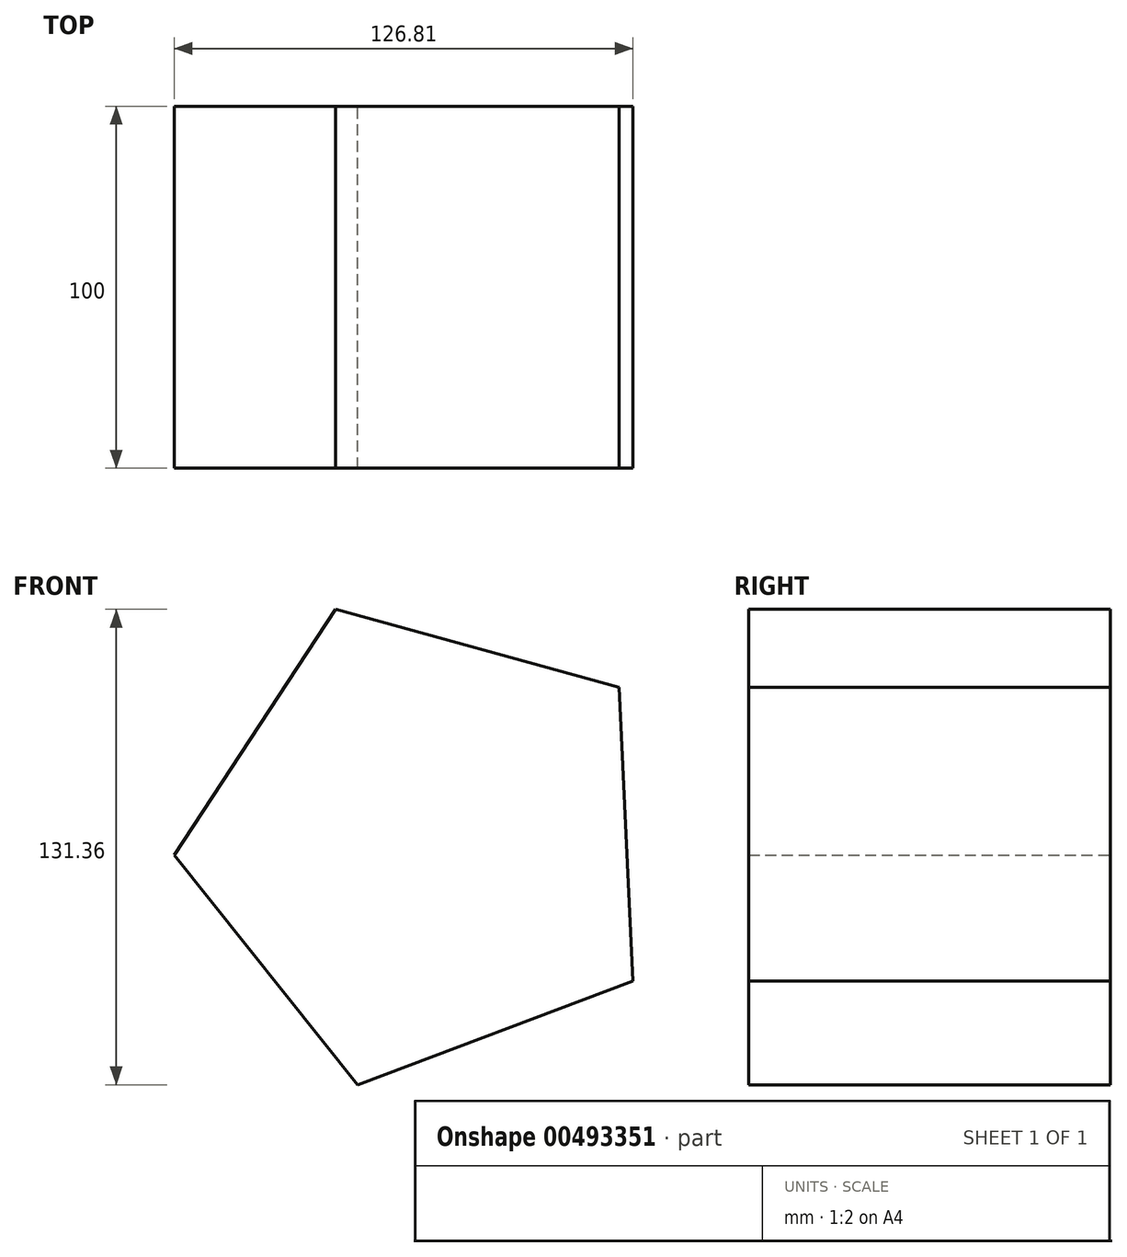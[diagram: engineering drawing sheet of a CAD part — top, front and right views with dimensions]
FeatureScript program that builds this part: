
annotation { "Feature Type Name" : "Feature", "Feature Type Description" : "" }
export const myFeature = defineFeature(function(context is Context, id is Id, definition is map)
    precondition{}
    {
        {
            var Q0;
            Q0=qCreatedBy(makeId("Front.planeOp"),FACE);
            var sketch = newSketch(context, id + "F0", { "sketchPlane" : qUnion([Q0])});
            skCircle(sketch, "E0.cCircle", {"center": v(0, 0) * mm, "radius": 69.14 * mm, "construction": true});
            skLineSegment(sketch, "E0.0", {"start": v(-24.39, 64.7) * mm, "end": v(54, 43.18) * mm});
            skLineSegment(sketch, "E0.1", {"start": v(54, 43.18) * mm, "end": v(57.75, -38) * mm});
            skLineSegment(sketch, "E0.2", {"start": v(57.75, -38) * mm, "end": v(-18.3, -66.67) * mm});
            skLineSegment(sketch, "E0.3", {"start": v(-18.3, -66.67) * mm, "end": v(-69.06, -3.2) * mm});
            skLineSegment(sketch, "E0.4", {"start": v(-69.06, -3.2) * mm, "end": v(-24.39, 64.7) * mm});
            skSolve(sketch);
        }
        {
            var Q0;
            Q0 = qSketchRegion(id + "F0", true);
            extrude(context, id + "F1", {"entities" : qUnion([Q0]), "endBound" : BoundingType.SYMMETRIC, "depth" : 100 * mm});
        }
    });
